# Revit family: Spaces In Between_Recharge-Energize
name_source: partatom
category: Furniture
units: mm (PartAtom-declared; Revit-internal decimal feet)

## family parameters
Always vertical = Yes
Cut with Voids When Loaded = No
OmniClass Number = 23.40.20.00
OmniClass Title = General Furniture and Specialties
Room Calculation Point = No
Shared = No
Work Plane-Based = No

## types (1)
- Spaces In Between_Recharge-Energize
    3" Rectangle Leg = <By Category>
    36" Round Ottoman Laminate Edge = <By Category>
    36" Round Ottoman Laminate Top = <By Category>
    36" Round Ottoman Seat Fabric = <By Category>
    36" Round Ottoman Side Fabric = <By Category>
    6" Rectangle Leg = <By Category>
    Arc Bench 60 - Small Seat Fabric- 1 = <By Category>
    Arc Bench 60 - Small Seat Fabric- 2 = <By Category>
    Arc Bench 60 - Small Side Fabric- 1 = <By Category>
    Arc Bench 60 - Small Side Fabric- 2 = <By Category>
    Glide = <By Category>
    Linear Corner Ottoman Seat Fabric = <By Category>
    Linear Corner Ottoman Side Fabric = <By Category>
    Linear Loveseat Back Fabric - 1 = <By Category>
    Linear Loveseat Back Fabric - 2 = <By Category>
    Linear Loveseat Seat Fabric - 1 = <By Category>
    Linear Loveseat Seat Fabric - 2 = <By Category>
    Manufacturer = FOMCORE
    Model = Spaces In Between_Recharge-Energize
    ROK Drop Ottoman Seat Fabric - 1 = <By Category>
    ROK Drop Ottoman Seat Fabric - 2 = <By Category>
    ROK Drop Ottoman Side Fabric - 1 = <By Category>
    ROK Drop Ottoman Side Fabric - 2 = <By Category>
    Sidekick Table Laminate Edge = <By Category>
    Sidekick Table Laminate Top = <By Category>
    Sled Leg29 = <By Category>
    Triangle Leg = <By Category>
    Type Comments = COMBO UNIT
    URL = https://fomcore.com

## geometry (parser evidence)
native form markers: Sweep x7
no freeform markers — native parametric forms only
